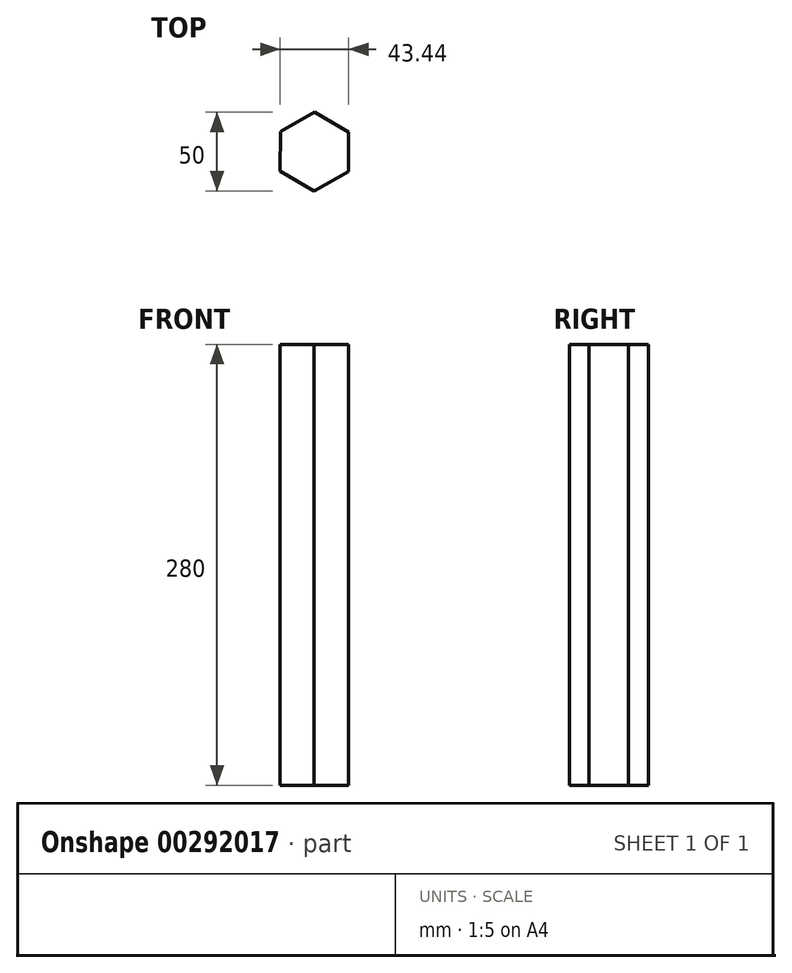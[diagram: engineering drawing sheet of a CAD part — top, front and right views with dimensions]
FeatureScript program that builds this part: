
annotation { "Feature Type Name" : "Feature", "Feature Type Description" : "" }
export const myFeature = defineFeature(function(context is Context, id is Id, definition is map)
    precondition{}
    {
        {
            var Q0;
            Q0=qCreatedBy(makeId("Top.planeOp"),FACE);
            var sketch = newSketch(context, id + "F0", { "sketchPlane" : qUnion([Q0])});
            skCircle(sketch, "E0.cCircle", {"center": v(0, 0) * mm, "radius": 21.65 * mm, "construction": true});
            skLineSegment(sketch, "E0.0", {"start": v(21.58, -12.62) * mm, "end": v(-0.14, -25) * mm});
            skLineSegment(sketch, "E0.1", {"start": v(-0.14, -25) * mm, "end": v(-21.72, -12.38) * mm});
            skLineSegment(sketch, "E0.2", {"start": v(-21.72, -12.38) * mm, "end": v(-21.58, 12.62) * mm});
            skLineSegment(sketch, "E0.3", {"start": v(-21.58, 12.62) * mm, "end": v(0.14, 25) * mm});
            skLineSegment(sketch, "E0.4", {"start": v(0.14, 25) * mm, "end": v(21.72, 12.38) * mm});
            skLineSegment(sketch, "E0.5", {"start": v(21.72, 12.38) * mm, "end": v(21.58, -12.62) * mm});
            skPoint(sketch, "E0.0.midPoint", {"position": v(10.72, -18.81) * mm});
            skSolve(sketch);
        }
        {
            var Q0;
            Q0=makeQuery(id+"F0.imprint","IMPRINT",FACE,{"disambiguationData":[TD([[makeQuery(id+"F0.imprint","IMPRINT",EDGE,{"derivedFrom":sQuery(id+"F0.wireOp",EDGE,"E0.0")}),-1.0]])]});
            extrude(context, id + "F1", {"entities" : qUnion([Q0]), "depth" : 280 * mm});
        }
    });
